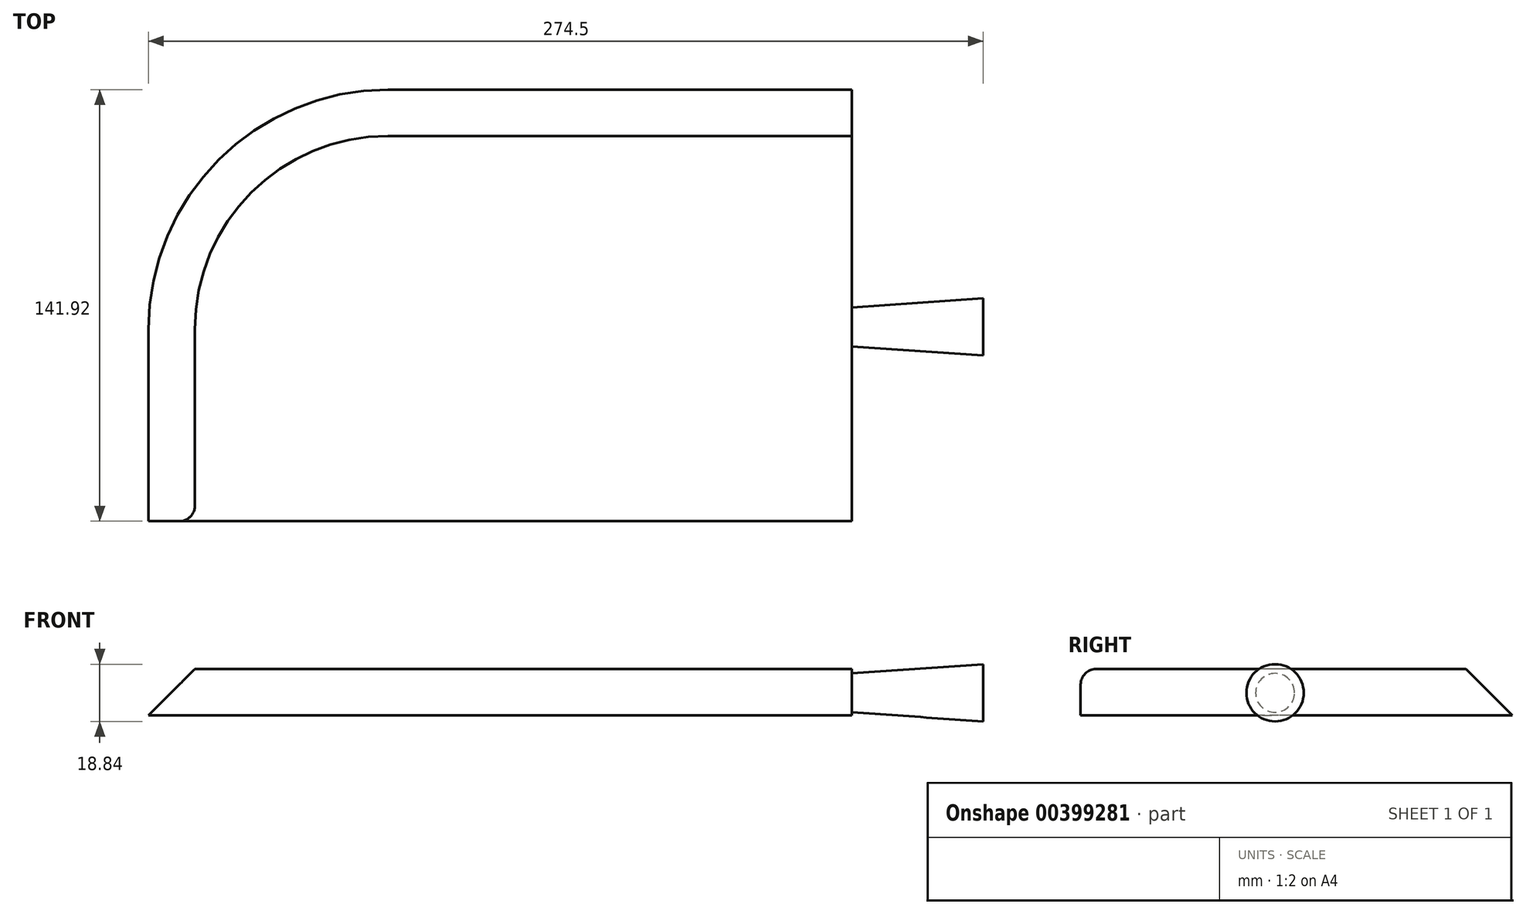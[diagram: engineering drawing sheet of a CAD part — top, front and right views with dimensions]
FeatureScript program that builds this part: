
annotation { "Feature Type Name" : "Feature", "Feature Type Description" : "" }
export const myFeature = defineFeature(function(context is Context, id is Id, definition is map)
    precondition{}
    {
        {
            var Q0;
            Q0=qCreatedBy(makeId("Top.planeOp"),FACE);
            var sketch = newSketch(context, id + "F0", { "sketchPlane" : qUnion([Q0])});
            skLineSegment(sketch, "E0.bottom", {"start": v(-31.84, 76.04) * mm, "end": v(120.74, 76.04) * mm});
            skLineSegment(sketch, "E0.top", {"start": v(-120.74, -76.04) * mm, "end": v(120.74, -76.04) * mm});
            skLineSegment(sketch, "E0.left", {"start": v(-120.74, -12.86) * mm, "end": v(-120.74, -76.04) * mm});
            skLineSegment(sketch, "E0.right", {"start": v(120.74, 76.04) * mm, "end": v(120.74, -76.04) * mm});
            skPoint(sketch, "E0.middle", {"position": v(0, 0) * mm});
            skPoint(sketch, "E1.visualSharp", {"position": v(-120.74, 76.04) * mm});
            skArc(sketch, "E1.filletArc", {"start": v(-31.84, 76.04) * mm, "mid": v(-94.7, 50) * mm, "end": v(-120.74, -12.86) * mm});
            skSolve(sketch);
        }
        {
            var Q0;
            Q0=makeQuery(id+"F0.imprint","IMPRINT",FACE,{"disambiguationData":[TD([[makeQuery(id+"F0.imprint","IMPRINT",EDGE,{"derivedFrom":sQuery(id+"F0.wireOp",EDGE,"E0.bottom")}),-1.0]])]});
            extrude(context, id + "F1", {"entities" : qUnion([Q0]), "depth" : 15.24 * mm});
        }
        {
            var Q0;
            Q0=makeQuery(id+"F1.opExtrude","CAP_EDGE",EDGE,{"disambiguationData":[OSD([sQuery(id+"F0.wireOp",EDGE,"E1.filletArc")])],"isStart":false});
            chamfer(context, id + "F2", {"entities" : qUnion([Q0]), "width" : 25.4 * mm, "tangentPropagation" : true});
        }
        {
            var Q0;
            Q0=makeQuery(id+"F1.opExtrude","CAP_EDGE",EDGE,{"disambiguationData":[OSD([sQuery(id+"F0.wireOp",EDGE,"E0.top")])],"isStart":false});
            fillet(context, id + "F3", {"entities" : qUnion([Q0]), "radius" : 5.08 * mm, "tangentPropagation" : true, "allowEdgeOverflow" : false});
        }
        {
            var Q0;
            Q0=makeQuery(id+"F1.opExtrude","SWEPT_FACE",FACE,{"disambiguationData":[OSD([sQuery(id+"F0.wireOp",EDGE,"E0.right")])]});
            var sketch = newSketch(context, id + "F4", { "sketchPlane" : qUnion([Q0])});
            skCircle(sketch, "E2", {"center": v(-12.12, 7.42) * mm, "radius": 6.4 * mm});
            skSolve(sketch);
        }
        {
            var Q0;
            Q0=makeQuery(id+"F4.imprint","IMPRINT",FACE,{"disambiguationData":[TD([[makeQuery(id+"F4.imprint","IMPRINT",EDGE,{"derivedFrom":sQuery(id+"F4.wireOp",EDGE,"E2")}),1.0]])]});
            extrude(context, id + "F5", {"entities" : qUnion([Q0]), "operationType" : NewBodyOperationType.ADD, "depth" : 43.18 * mm, "hasDraft" : true, "draftAngle" : 4 * degree});
        }
    });
